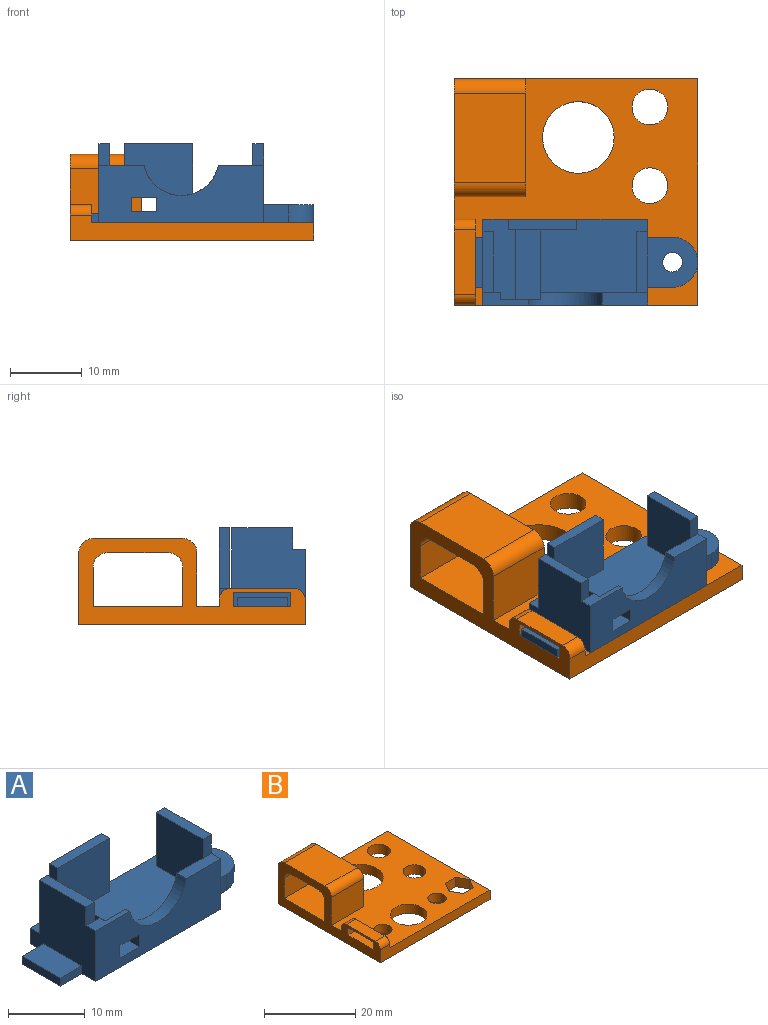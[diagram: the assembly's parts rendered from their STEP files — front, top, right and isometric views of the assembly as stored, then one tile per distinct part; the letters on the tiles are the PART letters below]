
ASSEMBLY  parts=2 mates=1
PART A: 40 faces, bbox 34x12x11 mm
  f0: plane 6.3x1.75mm, normal (0,0,1), area 7.2mm2, adj f1,f12,f13,f24,f30,f38,f39
  f1: plane 5.5x1mm, normal (0,1,0), area 5.5mm2, adj f0,f4,f25,f39
  f2: plane 4x1.25mm, normal (0,1,0), area 5mm2, adj f3,f12,f15,f37
  f3: plane 7x1.25mm, normal (-1,0,0), area 8.7mm2, adj f2,f11,f15,f37
  f4: plane 11.25x4.5mm, normal (0,0,1), area 33.9mm2, adj f1,f10,f12,f16,f17,f25,f26,f32
  f5: plane 15x10.25mm, normal (0,0,1), area 133.3mm2, adj f7,f10,f17,f18,f20,f21,f28,f35
  f6: plane 7x7mm, normal (0,0,1), area 37.8mm2, adj f7,f8,f9,f14,f36
  f7: plane 12x11mm, normal (1,0,0), area 94.4mm2, adj f5,f6,f8,f9,f10,f13,f15,f20
  f8: plane 3.5x2.5mm, normal (0,-1,0), area 8.7mm2, adj f6,f7,f15,f36
  f9: plane 3.5x2.5mm, normal (0,1,0), area 8.7mm2, adj f6,f7,f15,f36
  f10: plane 23x11mm, normal (0,1,0), area 132.1mm2, adj f4,f5,f7,f12,f15,f16,f18,f19
  f11: plane 4x1.25mm, normal (0,-1,0), area 5mm2, adj f3,f12,f15,f37
  f12: plane 12x11mm, normal (-1,0,0), area 103.1mm2, adj f0,f2,f4,f10,f11,f13,f15,f24
  f13: plane 23x8mm, normal (0,-1,0), area 143.9mm2, adj f0,f7,f12,f15,f29,f30,f31,f32
  f14: cylinder r=1.38mm len=2.75mm, axis (0,0,-1), area 21.6mm2, adj f6,f15
  f15: plane 34x12mm, normal (0,0,-1), area 341.8mm2, adj f2,f3,f7,f8,f9,f10,f11,f12
  f16: plane 8.5x1.5mm, normal (-1,0,0), area 12.7mm2, adj f4,f10,f17,f19
  f17: plane 9.6x8.5mm, normal (0,-1,0), area 78.1mm2, adj f4,f5,f16,f18,f19,f32,f34,f35
  f18: plane 8.5x1.5mm, normal (1,0,0), area 12.7mm2, adj f5,f10,f17,f19
  f19: plane 9.6x1.5mm, normal (0,0,1), area 14.4mm2, adj f10,f16,f17,f18
  f20: plane 8.5x1.5mm, normal (0,1,0), area 12.8mm2, adj f5,f7,f21,f23
  f21: plane 8.5x8.5mm, normal (-1,0,0), area 72.2mm2, adj f5,f20,f22,f23,f28
  f22: plane 3x1.5mm, normal (0,-1,0), area 4.5mm2, adj f7,f21,f23,f29
  f23: plane 8.5x1.5mm, normal (0,0,1), area 12.8mm2, adj f7,f20,f21,f22
  f24: plane 3x1.5mm, normal (0,-1,0), area 4.5mm2, adj f0,f12,f25,f27
  f25: plane 8.5x8.5mm, normal (1,0,0), area 72.2mm2, adj f1,f4,f24,f26,f27
  f26: plane 8.5x1.5mm, normal (0,1,0), area 12.7mm2, adj f4,f12,f25,f27
  f27: plane 8.5x1.5mm, normal (0,0,1), area 12.7mm2, adj f12,f24,f25,f26
  f28: plane 13.5x5.5mm, normal (0,1,0), area 44.3mm2, adj f5,f21,f29,f30,f35
  f29: plane 6.3x1.75mm, normal (0,0,1), area 11mm2, adj f7,f13,f22,f28,f30
  f30: cylinder r=5.31mm len=10.4mm, axis (0,-1,0), area 22mm2, adj f0,f13,f28,f29,f35,f38
  f31: plane 12x3.5mm, normal (0,0,1), area 42mm2, adj f10,f13,f32,f35
  f32: plane 12x2mm, normal (1,0,0), area 14.3mm2, adj f4,f10,f13,f17,f31,f33,f34,f38
  f33: plane 3.5x0.75mm, normal (0,0,-1), area 2.6mm2, adj f13,f32,f35,f38
  f34: plane 3.5x1.5mm, normal (0,0,-1), area 5.3mm2, adj f10,f17,f32,f35
  f35: plane 12x3.57mm, normal (-1,0,0), area 16.8mm2, adj f5,f10,f13,f17,f28,f30,f31,f33
  f36: cylinder r=3.5mm len=7mm, axis (0,0,-1), area 27.5mm2, adj f6,f8,f9,f15
  f37: plane 7x4mm, normal (0,0,1), area 28mm2, adj f2,f3,f11,f12
  f38: plane 5.5x5.5mm, normal (0,1,0), area 23.6mm2, adj f0,f4,f30,f32,f33,f35,f39
  f39: plane 5.5x1mm, normal (1,0,0), area 5.5mm2, adj f0,f1,f4,f38
PART B: 36 faces, bbox 34x31.6x12 mm
  f0: plane 12x2.5mm, normal (1,0,0), area 13mm2, adj f3,f4,f5,f6,f15,f16,f17,f28
  f1: plane 31.62x12mm, normal (-1,0,0), area 155.1mm2, adj f2,f3,f4,f5,f6,f7,f15,f16
  f2: plane 34x31.62mm, normal (0,0,-1), area 855.7mm2, adj f1,f4,f7,f8,f9,f10,f11,f12
  f3: plane 34x31.62mm, normal (0,0,1), area 803.7mm2, adj f0,f1,f4,f5,f7,f8,f9,f10
  f4: plane 34x3.5mm, normal (0,-1,0), area 88mm2, adj f0,f1,f2,f3,f8,f29
  f5: plane 3x1mm, normal (0,1,0), area 3mm2, adj f0,f1,f3,f28
  f6: plane 9x3mm, normal (0,0,1), area 27mm2, adj f0,f1,f28,f29
  f7: plane 34x10mm, normal (0,1,0), area 160mm2, adj f1,f2,f3,f8,f23,f26
  f8: plane 31.62x2.5mm, normal (1,0,0), area 79mm2, adj f2,f3,f4,f7
  f9: plane 2.75x2.5mm, normal (-0.87,0.5,0), area 7.9mm2, adj f2,f3,f10,f14
  f10: plane 2.75x2.5mm, normal (-0.87,-0.5,0), area 7.9mm2, adj f2,f3,f9,f11
  f11: plane 3.18x2.5mm, normal (0,-1,0), area 7.9mm2, adj f2,f3,f10,f12
  f12: plane 2.75x2.5mm, normal (0.87,-0.5,0), area 7.9mm2, adj f2,f3,f11,f13
  f13: plane 2.75x2.5mm, normal (0.87,0.5,0), area 7.9mm2, adj f2,f3,f12,f14
  f14: plane 3.18x2.5mm, normal (0,1,0), area 7.9mm2, adj f2,f3,f9,f13
  f15: plane 3x2mm, normal (0,-1,0), area 6mm2, adj f0,f1,f3,f17
  f16: plane 3x2mm, normal (0,1,0), area 6mm2, adj f0,f1,f3,f17
  f17: plane 8x3mm, normal (0,0,-1), area 24mm2, adj f0,f1,f15,f16
  f18: plane 12.5x10mm, normal (0,0,1), area 125mm2, adj f1,f23,f26,f27
  f19: plane 10x7.5mm, normal (0,-1,0), area 75mm2, adj f1,f3,f23,f27
  f20: plane 10x5.5mm, normal (0,1,0), area 55mm2, adj f1,f3,f23,f24
  f21: plane 10x8.5mm, normal (0,0,-1), area 85mm2, adj f1,f23,f24,f25
  f22: plane 10x5.5mm, normal (0,-1,0), area 55mm2, adj f1,f3,f23,f25
  f23: plane 16.5x9.5mm, normal (1,0,0), area 63mm2, adj f3,f7,f18,f19,f20,f21,f22,f24
  f24: cylinder r=2mm len=10mm, axis (1,0,0), area 31.4mm2, adj f1,f20,f21,f23
  f25: cylinder r=2mm len=10mm, axis (1,0,0), area 31.4mm2, adj f1,f21,f22,f23
  f26: cylinder r=2mm len=10mm, axis (1,0,0), area 31.4mm2, adj f1,f7,f18,f23
  f27: cylinder r=2mm len=10mm, axis (1,0,0), area 31.4mm2, adj f1,f18,f19,f23
  f28: cylinder r=1.5mm len=3mm, axis (1,0,0), area 7.1mm2, adj f0,f1,f5,f6
  f29: cylinder r=1.5mm len=3mm, axis (-1,0,0), area 7.1mm2, adj f0,f1,f4,f6
  f30: cylinder r=5mm len=10mm, axis (0,0,1), area 78.5mm2, adj f2,f3
  f31: cylinder r=2mm len=4mm, axis (0,0,1), area 31.4mm2, adj f2,f3
  f32: cylinder r=4mm len=8mm, axis (0,0,1), area 62.8mm2, adj f2,f3
  f33: cylinder r=2.5mm len=5mm, axis (0,0,1), area 39.3mm2, adj f2,f3
  f34: cylinder r=2.5mm len=5mm, axis (0,0,1), area 39.3mm2, adj f2,f3
  f35: cylinder r=2mm len=4mm, axis (0,0,1), area 31.4mm2, adj f2,f3
PLACE A t=(-1,-0.5,1.5)mm
PLACE B t=(-1,-0.5,-1)mm
MATE fastened A.f14 <-> B.f3  axis (0,0,-1) through (25.5,5.5,1.5)mm
